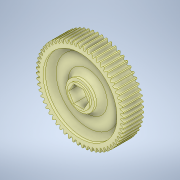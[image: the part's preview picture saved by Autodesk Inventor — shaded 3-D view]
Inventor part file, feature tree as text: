
AUTODESK INVENTOR PART (.ipt)
format: ipt  version: 2020 (Build 240168000, 168)  size: 704,000 bytes
history: native  units: in
note: dims shown in document units (in); Inventor stores cm internally (conversion verified against a paired STEP export)
features: mirror x1
ambient origin geometry x8: Origin, YZ Plane, XZ Plane, XY Plane, X Axis, Y Axis, Z Axis, Center Point
bodies: Solid1 (feature_tree)
feature tree (1):
  mirror  "Mirror1"
